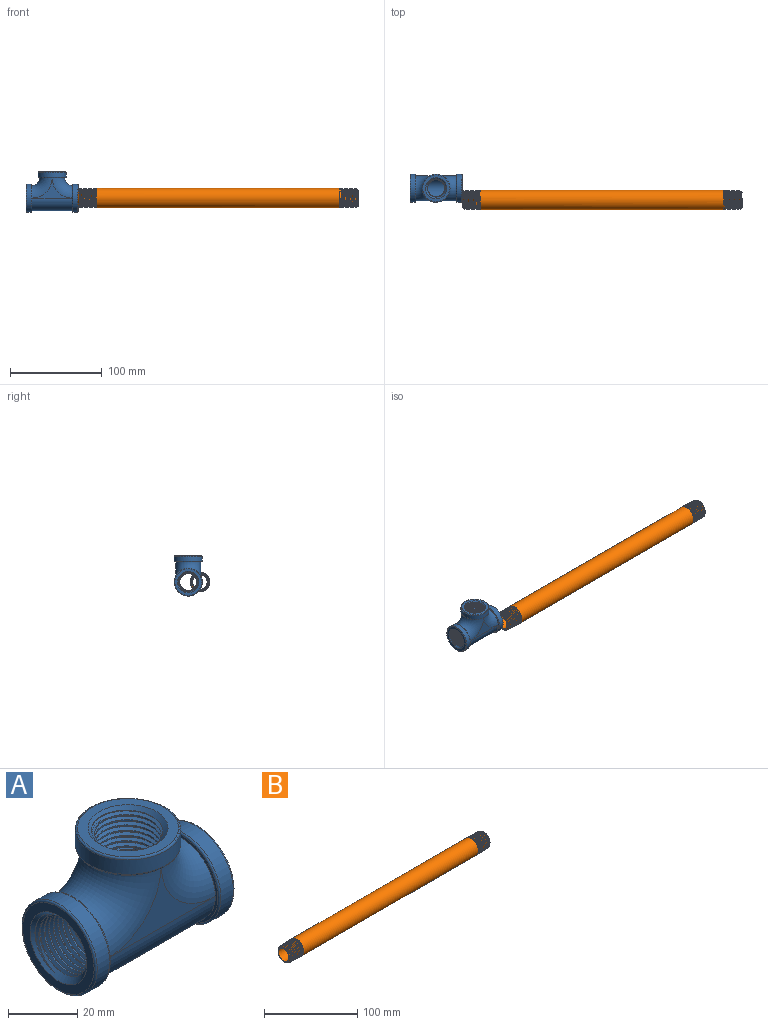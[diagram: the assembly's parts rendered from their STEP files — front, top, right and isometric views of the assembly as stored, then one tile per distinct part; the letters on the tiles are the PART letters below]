
ASSEMBLY  parts=2 mates=1
PART A: 43 faces, bbox 56.9x33x45 mm
  f0: torus R=13.97mm, axis (0,-1,0), area 377.9mm2, adj f38,f39,f41,f42
  f1: torus R=13.97mm, axis (0,1,0), area 377.9mm2, adj f38,f40,f41,f42
  f2: cylinder r=10.67mm len=27.94mm, axis (-1,0,0), area 936.4mm2, adj f39,f40,f41,f42
  f3: plane 29.21x29.21mm, normal (1,0,0), area 249.2mm2, adj f27,f33
  f4: plane 29.21x29.21mm, normal (-1,0,0), area 249.2mm2, adj f25,f28
  f5: plane 29.21x29.21mm, normal (0,0,1), area 249.2mm2, adj f14,f15
  f6: torus R=22.1mm, axis (0,1,0), area 901.7mm2, adj f9,f10,f12,f20
  f7: cylinder r=13.59mm len=44.2mm, axis (-1,0,0), area 1886.8mm2, adj f9,f10,f20,f22
  f8: torus R=22.1mm, axis (0,1,0), area 901.7mm2, adj f9,f10,f12,f22
  f9: plane 44.2x22.1mm, normal (0,1,0), area 209.6mm2, adj f6,f7,f8
  f10: plane 44.2x22.1mm, normal (0,-1,0), area 209.6mm2, adj f6,f7,f8
  f11: cylinder r=15.24mm len=30.48mm, axis (0,0,-1), area 486.4mm2, adj f13,f14
  f12: plane 29.21x29.21mm, normal (0,0,-1), area 90mm2, adj f6,f8,f13
  f13: torus R=14.61mm, axis (0,0,-1), area 94.1mm2, adj f11,f12
  f14: torus R=14.61mm, axis (0,0,1), area 94.1mm2, adj f5,f11
  f15: cone r=11.58mm half-angle=45deg, axis (0,0,1), area 142.4mm2, adj f5,f16,f17,f18,f19
  f16: bspline ~19.56x19.5mm, area 186.4mm2, adj f15,f17,f18,f38
  f17: bspline ~21.94x21.89mm, area 510.1mm2, adj f15,f16,f19,f38
  f18: bspline ~21.64x21.59mm, area 486mm2, adj f15,f16,f19,f38
  f19: cone r=10.67mm half-angle=1.8deg, axis (0,0,1), area 97.5mm2, adj f15,f17,f18,f38
  f20: plane 29.21x29.21mm, normal (1,0,0), area 90mm2, adj f6,f7,f24
  f21: cylinder r=15.24mm len=30.48mm, axis (1,0,0), area 486.4mm2, adj f24,f25
  f22: plane 29.21x29.21mm, normal (-1,0,0), area 90mm2, adj f7,f8,f26
  f23: cylinder r=15.24mm len=30.48mm, axis (-1,0,0), area 486.4mm2, adj f26,f27
  f24: torus R=14.61mm, axis (1,0,0), area 94.1mm2, adj f20,f21
  f25: torus R=14.61mm, axis (1,0,0), area 94.1mm2, adj f4,f21
  f26: torus R=14.61mm, axis (-1,0,0), area 94.1mm2, adj f22,f23
  f27: torus R=14.61mm, axis (-1,0,0), area 94.1mm2, adj f3,f23
  f28: cone r=11.58mm half-angle=45deg, axis (-1,0,0), area 142.4mm2, adj f4,f29,f30,f31,f32
  f29: bspline ~19.56x19.5mm, area 186.4mm2, adj f28,f30,f31,f39
  f30: bspline ~21.94x21.89mm, area 510.1mm2, adj f28,f29,f32,f39
  f31: bspline ~21.64x21.59mm, area 486mm2, adj f28,f29,f32,f39
  f32: cone r=10.67mm half-angle=1.8deg, axis (-1,0,0), area 97.5mm2, adj f28,f30,f31,f39
  f33: cone r=11.58mm half-angle=45deg, axis (1,0,0), area 142.4mm2, adj f3,f34,f35,f36,f37
  f34: bspline ~19.56x19.5mm, area 186.4mm2, adj f33,f35,f36,f40
  f35: bspline ~21.94x21.89mm, area 510.1mm2, adj f33,f34,f37,f40
  f36: bspline ~21.64x21.59mm, area 486mm2, adj f33,f34,f37,f40
  f37: cone r=10.67mm half-angle=1.8deg, axis (1,0,0), area 97.5mm2, adj f33,f35,f36,f40
  f38: plane 21.36x21.36mm, normal (0,0,-1), area 62.4mm2, adj f0,f1,f16,f17,f18,f19
  f39: plane 21.36x21.36mm, normal (1,0,0), area 62.4mm2, adj f0,f2,f29,f30,f31,f32
  f40: plane 21.36x21.36mm, normal (-1,0,0), area 62.4mm2, adj f1,f2,f34,f35,f36,f37
  f41: plane 27.94x13.97mm, normal (0,-1,0), area 83.8mm2, adj f0,f1,f2
  f42: plane 27.94x13.97mm, normal (0,1,0), area 83.8mm2, adj f0,f1,f2
PART B: 16 faces, bbox 306.4x22.1x22 mm
  f0: plane 17.38x17.38mm, normal (-1,0,0), area 41.2mm2, adj f3,f15
  f1: plane 17.38x17.38mm, normal (1,0,0), area 41.2mm2, adj f10,f15
  f2: cone r=10.67mm half-angle=1.8deg, axis (1,0,0), area 134.4mm2, adj f3,f4,f5,f8
  f3: cone r=10.09mm half-angle=45deg, axis (1,0,0), area 63.1mm2, adj f0,f2,f4,f5,f6
  f4: bspline ~21.94x21.9mm, area 849.2mm2, adj f2,f3,f6,f7
  f5: bspline ~22.05x22.01mm, area 814.6mm2, adj f2,f3,f6,f7
  f6: bspline ~19.03x18.94mm, area 121.1mm2, adj f3,f4,f5,f7
  f7: cone r=10.67mm half-angle=25deg, axis (1,0,0), area 99.2mm2, adj f4,f5,f6,f8
  f8: cylinder r=10.67mm len=265.1mm, axis (-1,0,0), area 17769.4mm2, adj f2,f7,f9,f14
  f9: cone r=10.67mm half-angle=1.8deg, axis (-1,0,0), area 134.4mm2, adj f8,f10,f11,f12
  f10: cone r=10.09mm half-angle=45deg, axis (-1,0,0), area 63.1mm2, adj f1,f9,f11,f12,f13
  f11: bspline ~21.94x21.9mm, area 849.2mm2, adj f9,f10,f13,f14
  f12: bspline ~22.05x22.01mm, area 814.6mm2, adj f9,f10,f13,f14
  f13: bspline ~19.03x18.94mm, area 121.1mm2, adj f10,f11,f12,f14
  f14: cone r=10.67mm half-angle=25deg, axis (-1,0,0), area 99.2mm2, adj f8,f11,f12,f13
  f15: cylinder r=7.9mm len=304.8mm, axis (1,0,0), area 15128.3mm2, adj f0,f1
PLACE A t=(-71.94,0,-2.22)mm
PLACE B t=(108.9,-12.7,-2.22)mm
MATE fastened B.f2 <-> A.f3  axis (-1,0,0) through (-43.5,-12.7,-2.22)mm
